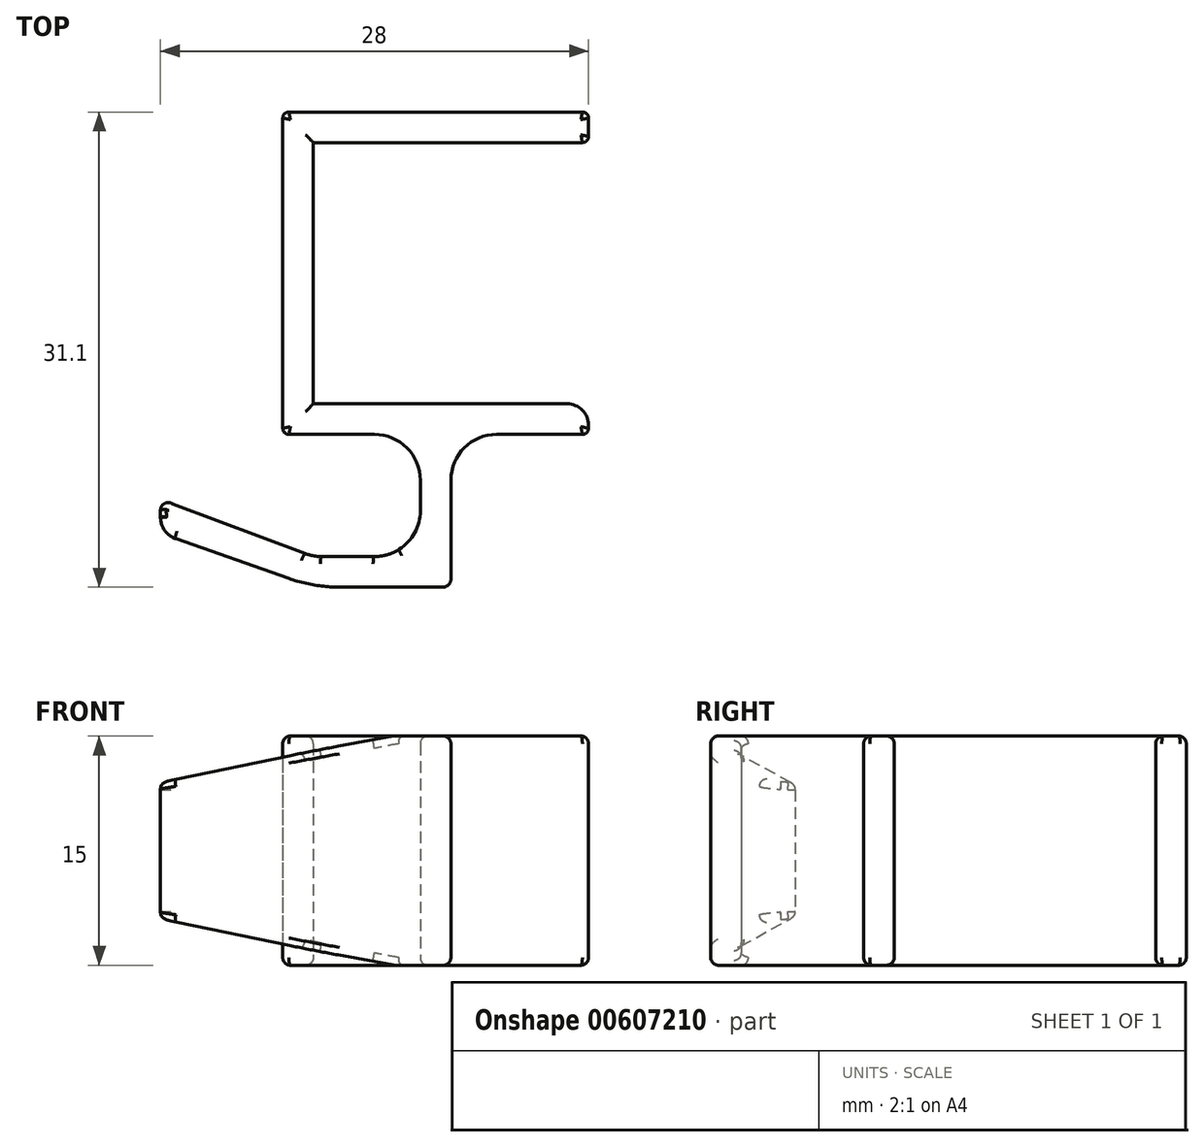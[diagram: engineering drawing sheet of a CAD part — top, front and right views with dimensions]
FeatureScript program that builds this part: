
annotation { "Feature Type Name" : "Feature", "Feature Type Description" : "" }
export const myFeature = defineFeature(function(context is Context, id is Id, definition is map)
    precondition{}
    {
        {
            var Q0;
            Q0=qCreatedBy(makeId("Top.planeOp"),FACE);
            var sketch = newSketch(context, id + "F0", { "sketchPlane" : qUnion([Q0])});
            skLineSegment(sketch, "E0.top", {"start": v(0, -8.55) * mm, "end": v(18, -8.55) * mm});
            skLineSegment(sketch, "E0.left", {"start": v(0, 8.55) * mm, "end": v(0, -8.55) * mm});
            skLineSegment(sketch, "E1.top", {"start": v(17.6, 10.55) * mm, "end": v(-1.6, 10.55) * mm});
            skLineSegment(sketch, "E1.left", {"start": v(18, 8.95) * mm, "end": v(18, 10.15) * mm});
            skLineSegment(sketch, "E2.bottom", {"start": v(16.6, -8.55) * mm, "end": v(0, -8.55) * mm});
            skLineSegment(sketch, "E2.top", {"start": v(17.6, -10.55) * mm, "end": v(12, -10.55) * mm});
            skLineSegment(sketch, "E2.left", {"start": v(18, -9.95) * mm, "end": v(18, -10.15) * mm});
            skLineSegment(sketch, "E3", {"start": v(-2, 10.15) * mm, "end": v(-2, -10.15) * mm});
            skLineSegment(sketch, "E4", {"start": v(0, 8.55) * mm, "end": v(17.6, 8.55) * mm});
            skLineSegment(sketch, "E5", {"start": v(0, 0) * mm, "end": v(-2, 0) * mm, "construction": true});
            skLineSegment(sketch, "E6", {"start": v(7, -13.55) * mm, "end": v(7, -15.55) * mm});
            skLineSegment(sketch, "E7", {"start": v(7, -20.55) * mm, "end": v(8.5, -20.55) * mm});
            skLineSegment(sketch, "E8", {"start": v(9, -20.05) * mm, "end": v(9, -13.55) * mm});
            skLineSegment(sketch, "E9.trimOffspring", {"start": v(4, -10.55) * mm, "end": v(-1.6, -10.55) * mm});
            skLineSegment(sketch, "E10", {"start": v(8, -9.55) * mm, "end": v(8, -20.55) * mm, "construction": true});
            skLineSegment(sketch, "E11", {"start": v(18, -9.55) * mm, "end": v(-2, -9.55) * mm, "construction": true});
            skLineSegment(sketch, "E12", {"start": v(7, -20.55) * mm, "end": v(1.7, -20.55) * mm});
            skLineSegment(sketch, "E13", {"start": v(-1.61, -19.98) * mm, "end": v(-9, -17.39) * mm});
            skLineSegment(sketch, "E14", {"start": v(-10, -15.97) * mm, "end": v(-10, -15.52) * mm});
            skLineSegment(sketch, "E15", {"start": v(-9.32, -15.05) * mm, "end": v(-0.5, -18.36) * mm});
            skLineSegment(sketch, "E16", {"start": v(0.54, -18.55) * mm, "end": v(4, -18.55) * mm});
            skLineSegment(sketch, "E17", {"start": v(-5, -16.67) * mm, "end": v(-5.7, -18.54) * mm, "construction": true});
            skLineSegment(sketch, "E18", {"start": v(3.5, -18.55) * mm, "end": v(3.5, -20.55) * mm, "construction": true});
            skLineSegment(sketch, "E19", {"start": v(-10, -14.8) * mm, "end": v(0, -14.8) * mm, "construction": true});
            skLineSegment(sketch, "E20", {"start": v(0, -14.8) * mm, "end": v(0, -18.55) * mm, "construction": true});
            skPoint(sketch, "E21.visualSharp", {"position": v(18, 10.55) * mm});
            skArc(sketch, "E21.filletArc", {"start": v(18, 10.15) * mm, "mid": v(17.88, 10.43) * mm, "end": v(17.6, 10.55) * mm});
            skPoint(sketch, "E22.visualSharp", {"position": v(18, 8.55) * mm});
            skArc(sketch, "E22.filletArc", {"start": v(17.6, 8.55) * mm, "mid": v(17.88, 8.67) * mm, "end": v(18, 8.95) * mm});
            skPoint(sketch, "E23.visualSharp", {"position": v(-2, 10.55) * mm});
            skArc(sketch, "E23.filletArc", {"start": v(-1.6, 10.55) * mm, "mid": v(-1.88, 10.43) * mm, "end": v(-2, 10.15) * mm});
            skPoint(sketch, "E24.visualSharp", {"position": v(-2, -10.55) * mm});
            skArc(sketch, "E24.filletArc", {"start": v(-2, -10.15) * mm, "mid": v(-1.88, -10.43) * mm, "end": v(-1.6, -10.55) * mm});
            skPoint(sketch, "E25.visualSharp", {"position": v(18, -8.55) * mm});
            skArc(sketch, "E25.filletArc", {"start": v(18, -9.95) * mm, "mid": v(17.59, -8.96) * mm, "end": v(16.6, -8.55) * mm});
            skPoint(sketch, "E26.visualSharp", {"position": v(18, -10.55) * mm});
            skArc(sketch, "E26.filletArc", {"start": v(17.6, -10.55) * mm, "mid": v(17.88, -10.43) * mm, "end": v(18, -10.15) * mm});
            skPoint(sketch, "E27.visualSharp", {"position": v(9, -10.55) * mm});
            skArc(sketch, "E27.filletArc", {"start": v(12, -10.55) * mm, "mid": v(9.88, -11.43) * mm, "end": v(9, -13.55) * mm});
            skPoint(sketch, "E28.visualSharp", {"position": v(7, -10.55) * mm});
            skArc(sketch, "E28.filletArc", {"start": v(7, -13.55) * mm, "mid": v(6.12, -11.43) * mm, "end": v(4, -10.55) * mm});
            skPoint(sketch, "E29.visualSharp", {"position": v(7, -18.55) * mm});
            skArc(sketch, "E29.filletArc", {"start": v(4, -18.55) * mm, "mid": v(6.12, -17.67) * mm, "end": v(7, -15.55) * mm});
            skPoint(sketch, "E30.visualSharp", {"position": v(0, -18.55) * mm});
            skArc(sketch, "E30.filletArc", {"start": v(-0.5, -18.36) * mm, "mid": v(0, -18.5) * mm, "end": v(0.54, -18.55) * mm});
            skPoint(sketch, "E31.visualSharp", {"position": v(0, -20.55) * mm});
            skArc(sketch, "E31.filletArc", {"start": v(-1.61, -19.98) * mm, "mid": v(0.02, -20.4) * mm, "end": v(1.7, -20.55) * mm});
            skPoint(sketch, "E32.visualSharp", {"position": v(9, -20.55) * mm});
            skArc(sketch, "E32.filletArc", {"start": v(8.5, -20.55) * mm, "mid": v(8.85, -20.4) * mm, "end": v(9, -20.05) * mm});
            skPoint(sketch, "E33.visualSharp", {"position": v(-10, -14.8) * mm});
            skArc(sketch, "E33.filletArc", {"start": v(-9.32, -15.05) * mm, "mid": v(-9.78, -15.1) * mm, "end": v(-10, -15.52) * mm});
            skPoint(sketch, "E34.visualSharp", {"position": v(-10, -17.03) * mm});
            skArc(sketch, "E34.filletArc", {"start": v(-10, -15.97) * mm, "mid": v(-9.72, -16.84) * mm, "end": v(-9, -17.39) * mm});
            skSolve(sketch);
        }
        {
            var Q0;
            Q0=makeQuery(id+"F0.imprint","IMPRINT",FACE,{"disambiguationData":[TD([[makeQuery(id+"F0.imprint","IMPRINT",EDGE,{"derivedFrom":sQuery(id+"F0.wireOp",EDGE,"E0.left")}),-1.0]])]});
            extrude(context, id + "F1", {"entities" : qUnion([Q0]), "depth" : 15 * mm, "offsetDistance" : 25 * mm});
        }
        {
            var Q0;
            Q0=makeQuery(id+"F1.opExtrude","SWEPT_FACE",FACE,{"disambiguationData":[OSD([sQuery(id+"F0.wireOp",EDGE,"E13")])]});
            var sketch = newSketch(context, id + "F2", { "sketchPlane" : qUnion([Q0])});
            skLineSegment(sketch, "E35.bottom", {"start": v(11.63, 15) * mm, "end": v(-6.37, 15) * mm});
            skLineSegment(sketch, "E35.top", {"start": v(11.63, 0) * mm, "end": v(-6.37, 0) * mm});
            skLineSegment(sketch, "E35.left", {"start": v(11.63, 15) * mm, "end": v(11.63, 0) * mm, "construction": true});
            skLineSegment(sketch, "E35.right", {"start": v(-6.37, 15) * mm, "end": v(-6.37, 11.5) * mm, "construction": true});
            skLineSegment(sketch, "E36", {"start": v(11.63, 15) * mm, "end": v(-3.75, 12) * mm});
            skLineSegment(sketch, "E37", {"start": v(-6.37, 11.5) * mm, "end": v(-6.37, 15) * mm});
            skLineSegment(sketch, "E38", {"start": v(11.63, 0) * mm, "end": v(-3.75, 3) * mm});
            skLineSegment(sketch, "E39", {"start": v(-6.37, 3.5) * mm, "end": v(-6.37, 0) * mm});
            skLineSegment(sketch, "E40.trimOffspring", {"start": v(-6.37, 3.5) * mm, "end": v(-6.37, 0) * mm, "construction": true});
            skLineSegment(sketch, "E41", {"start": v(11.63, 7.5) * mm, "end": v(-6.37, 7.5) * mm, "construction": true});
            skLineSegment(sketch, "E42", {"start": v(-6.37, 11.5) * mm, "end": v(-6.37, 3.5) * mm, "construction": true});
            skLineSegment(sketch, "E43.bottom", {"start": v(-6.37, 15) * mm, "end": v(-5.37, 15) * mm});
            skLineSegment(sketch, "E43.top", {"start": v(-6.37, 0) * mm, "end": v(-5.37, 0) * mm});
            skLineSegment(sketch, "E43.left", {"start": v(-6.37, 15) * mm, "end": v(-6.37, 0) * mm});
            skLineSegment(sketch, "E43.right", {"start": v(-5.37, 10.05) * mm, "end": v(-5.37, 4.95) * mm});
            skPoint(sketch, "E44.visualSharp", {"position": v(-5.37, 11.7) * mm});
            skArc(sketch, "E44.filletArc", {"start": v(-3.75, 12) * mm, "mid": v(-4.91, 11.32) * mm, "end": v(-5.37, 10.05) * mm});
            skPoint(sketch, "E45.visualSharp", {"position": v(-5.37, 3.3) * mm});
            skArc(sketch, "E45.filletArc", {"start": v(-5.37, 4.95) * mm, "mid": v(-4.91, 3.68) * mm, "end": v(-3.75, 3) * mm});
            skSolve(sketch);
        }
        {
            var Q0;
            Q0 = qSketchRegion(id + "F2", true);
            extrude(context, id + "F3", {"entities" : qUnion([Q0]), "operationType" : NewBodyOperationType.REMOVE, "oppositeDirection" : true, "depth" : 7 * mm, "offsetDistance" : 25 * mm});
        }
        {
            var Q0;
            Q0=makeQuery(id+"F1.opExtrude","CAP_EDGE",EDGE,{"disambiguationData":[OSD([sQuery(id+"F0.wireOp",EDGE,"E0.left")])],"isStart":false});
            var Q1;
            Q1=makeQuery(id+"F1.opExtrude","CAP_FACE",FACE,{"disambiguationData":[OSD([sQuery(id+"F0.wireOp",EDGE,"E0.left"),sQuery(id+"F0.wireOp",EDGE,"E1.top"),sQuery(id+"F0.wireOp",EDGE,"E1.left"),sQuery(id+"F0.wireOp",EDGE,"E2.bottom"),sQuery(id+"F0.wireOp",EDGE,"E2.top"),sQuery(id+"F0.wireOp",EDGE,"E2.left"),sQuery(id+"F0.wireOp",EDGE,"E3"),sQuery(id+"F0.wireOp",EDGE,"E4"),sQuery(id+"F0.wireOp",EDGE,"E6"),sQuery(id+"F0.wireOp",EDGE,"E7"),sQuery(id+"F0.wireOp",EDGE,"E8"),sQuery(id+"F0.wireOp",EDGE,"E9.trimOffspring"),sQuery(id+"F0.wireOp",EDGE,"E12"),sQuery(id+"F0.wireOp",EDGE,"E13"),sQuery(id+"F0.wireOp",EDGE,"E14"),sQuery(id+"F0.wireOp",EDGE,"E15"),sQuery(id+"F0.wireOp",EDGE,"E16"),sQuery(id+"F0.wireOp",EDGE,"E21.filletArc"),sQuery(id+"F0.wireOp",EDGE,"E22.filletArc"),sQuery(id+"F0.wireOp",EDGE,"E23.filletArc"),sQuery(id+"F0.wireOp",EDGE,"E24.filletArc"),sQuery(id+"F0.wireOp",EDGE,"E25.filletArc"),sQuery(id+"F0.wireOp",EDGE,"E26.filletArc"),sQuery(id+"F0.wireOp",EDGE,"E27.filletArc"),sQuery(id+"F0.wireOp",EDGE,"E28.filletArc"),sQuery(id+"F0.wireOp",EDGE,"E29.filletArc"),sQuery(id+"F0.wireOp",EDGE,"E30.filletArc"),sQuery(id+"F0.wireOp",EDGE,"E31.filletArc"),sQuery(id+"F0.wireOp",EDGE,"E32.filletArc"),sQuery(id+"F0.wireOp",EDGE,"E33.filletArc"),sQuery(id+"F0.wireOp",EDGE,"E34.filletArc")])],"isStart":false});
            var Q2;
            Q2=makeQuery(id+"F3.boolean.opBoolean","COPY",FACE,{"derivedFrom":makeQuery(id+"F3.opExtrude","SWEPT_FACE",FACE,{"disambiguationData":[OSD([sQuery(id+"F2.wireOp",EDGE,"E36")])]})});
            var Q3;
            Q3=makeQuery(id+"F1.opExtrude","CAP_FACE",FACE,{"disambiguationData":[OSD([sQuery(id+"F0.wireOp",EDGE,"E0.left"),sQuery(id+"F0.wireOp",EDGE,"E1.top"),sQuery(id+"F0.wireOp",EDGE,"E1.left"),sQuery(id+"F0.wireOp",EDGE,"E2.bottom"),sQuery(id+"F0.wireOp",EDGE,"E2.top"),sQuery(id+"F0.wireOp",EDGE,"E2.left"),sQuery(id+"F0.wireOp",EDGE,"E3"),sQuery(id+"F0.wireOp",EDGE,"E4"),sQuery(id+"F0.wireOp",EDGE,"E6"),sQuery(id+"F0.wireOp",EDGE,"E7"),sQuery(id+"F0.wireOp",EDGE,"E8"),sQuery(id+"F0.wireOp",EDGE,"E9.trimOffspring"),sQuery(id+"F0.wireOp",EDGE,"E12"),sQuery(id+"F0.wireOp",EDGE,"E13"),sQuery(id+"F0.wireOp",EDGE,"E14"),sQuery(id+"F0.wireOp",EDGE,"E15"),sQuery(id+"F0.wireOp",EDGE,"E16"),sQuery(id+"F0.wireOp",EDGE,"E21.filletArc"),sQuery(id+"F0.wireOp",EDGE,"E22.filletArc"),sQuery(id+"F0.wireOp",EDGE,"E23.filletArc"),sQuery(id+"F0.wireOp",EDGE,"E24.filletArc"),sQuery(id+"F0.wireOp",EDGE,"E25.filletArc"),sQuery(id+"F0.wireOp",EDGE,"E26.filletArc"),sQuery(id+"F0.wireOp",EDGE,"E27.filletArc"),sQuery(id+"F0.wireOp",EDGE,"E28.filletArc"),sQuery(id+"F0.wireOp",EDGE,"E29.filletArc"),sQuery(id+"F0.wireOp",EDGE,"E30.filletArc"),sQuery(id+"F0.wireOp",EDGE,"E31.filletArc"),sQuery(id+"F0.wireOp",EDGE,"E32.filletArc"),sQuery(id+"F0.wireOp",EDGE,"E33.filletArc"),sQuery(id+"F0.wireOp",EDGE,"E34.filletArc")])],"isStart":true});
            var Q4;
            Q4=makeQuery(id+"F3.boolean.opBoolean","COPY",FACE,{"derivedFrom":makeQuery(id+"F3.opExtrude","SWEPT_FACE",FACE,{"disambiguationData":[OSD([sQuery(id+"F2.wireOp",EDGE,"E38")])]})});
            fillet(context, id + "F4", {"entities" : qUnion([Q0, Q1, Q2, Q3, Q4]), "radius" : .5 * mm, "tangentPropagation" : true, "allowEdgeOverflow" : false});
        }
    });
